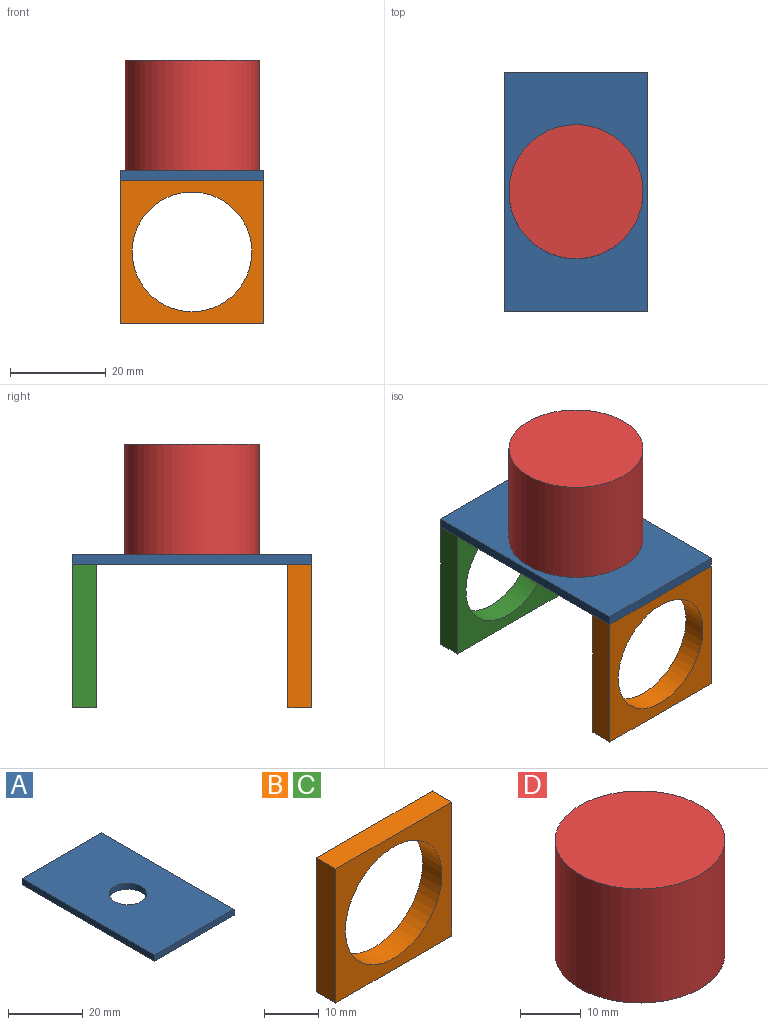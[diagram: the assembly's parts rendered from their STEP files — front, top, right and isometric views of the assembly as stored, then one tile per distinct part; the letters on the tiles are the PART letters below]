
ASSEMBLY  parts=4 mates=8
PART A: 7 faces, bbox 30x50x2 mm
  f0: plane 50x30mm, normal (0,0,1), area 1421.5mm2, adj f1,f3,f4,f5,f6
  f1: plane 50x2mm, normal (-1,0,0), area 100mm2, adj f0,f2,f4,f5
  f2: plane 50x30mm, normal (0,0,-1), area 1421.5mm2, adj f1,f3,f4,f5,f6
  f3: plane 50x2mm, normal (1,0,0), area 100mm2, adj f0,f2,f4,f5
  f4: plane 30x2mm, normal (0,-1,0), area 60mm2, adj f0,f1,f2,f3
  f5: plane 30x2mm, normal (0,1,0), area 60mm2, adj f0,f1,f2,f3
  f6: cylinder r=5mm len=10mm, axis (0,0,1), area 62.8mm2, adj f0,f2
PART B: 7 faces, bbox 30x5x30 mm
  f0: plane 30x5mm, normal (-1,0,0), area 150mm2, adj f1,f3,f4,f5
  f1: plane 30x30mm, normal (0,1,0), area 409.1mm2, adj f0,f2,f4,f5,f6
  f2: plane 30x5mm, normal (1,0,0), area 150mm2, adj f1,f3,f4,f5
  f3: plane 30x30mm, normal (0,-1,0), area 409.1mm2, adj f0,f2,f4,f5,f6
  f4: plane 30x5mm, normal (0,0,-1), area 150mm2, adj f0,f1,f2,f3
  f5: plane 30x5mm, normal (0,0,1), area 150mm2, adj f0,f1,f2,f3
  f6: cylinder r=12.5mm len=25mm, axis (0,-1,0), area 392.7mm2, adj f1,f3
PART C: same geometry as B
PART D: 3 faces, bbox 28x28x23 mm
  f0: cylinder r=14mm len=28mm, axis (0,0,-1), area 2023.2mm2, adj f1,f2
  f1: plane 28x28mm, normal (0,0,1), area 615.8mm2, adj f0
  f2: plane 28x28mm, normal (0,0,-1), area 615.8mm2, adj f0
PLACE A t=(-3.15,0.43,-8.51)mm
PLACE B t=(-3.15,0.43,-8.51)mm
PLACE C t=(-3.15,45.43,-8.51)mm
PLACE D t=(-3.15,0.43,4.99)mm
MATE planar B.f3 <-> A.f4  axis (0,-1,0) through (-3.15,-24.57,-8.51)mm
MATE planar C.f2 <-> A.f3  axis (1,0,0) through (11.85,22.93,-23.51)mm
MATE planar C.f5 <-> A.f6  axis (0,0,1) through (-3.15,25.43,-8.51)mm
MATE planar B.f5 <-> A.f6  axis (0,0,1) through (-3.15,-22.07,-8.51)mm
MATE planar A.f6 <-> D.f0  axis (0,0,1) through (-3.15,0.43,-6.51)mm
MATE planar A.f3 <-> B.f2  axis (1,0,0) through (11.85,0.43,-7.51)mm
MATE cylindrical D.f0 <-> A.f6  axis (0,0,-1) through (-3.15,0.43,4.99)mm
MATE planar C.f6 <-> A.f5  axis (0,1,0) through (-3.15,25.43,-23.51)mm
